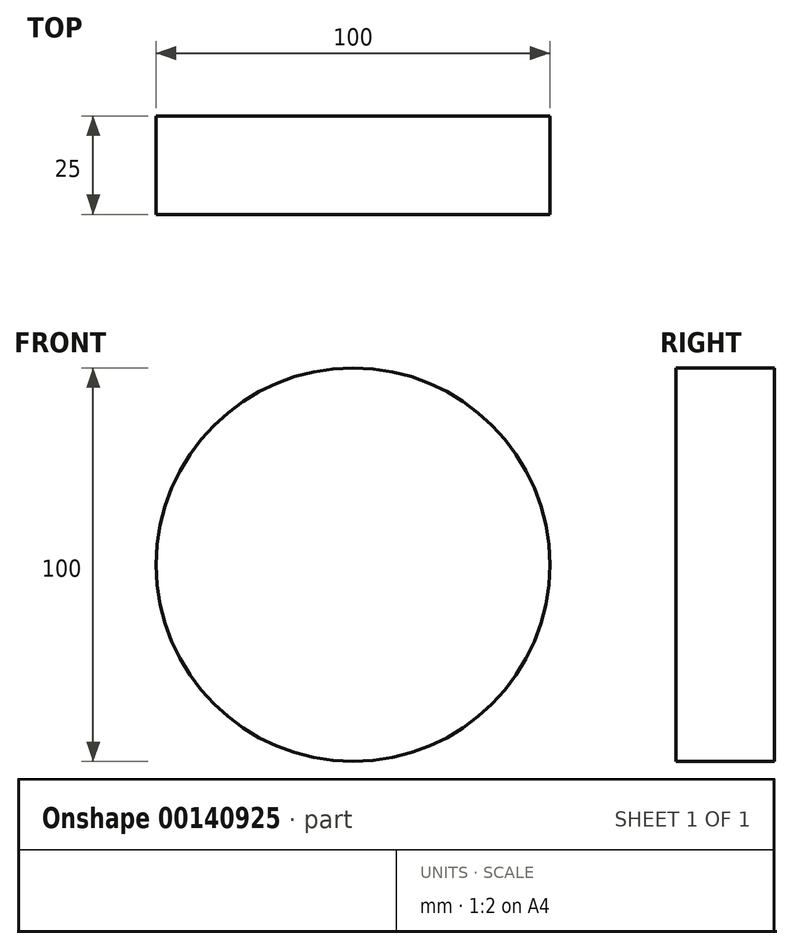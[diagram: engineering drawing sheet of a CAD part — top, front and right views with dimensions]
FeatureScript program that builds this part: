
annotation { "Feature Type Name" : "Feature", "Feature Type Description" : "" }
export const myFeature = defineFeature(function(context is Context, id is Id, definition is map)
    precondition{}
    {
        {
            var Q0;
            Q0=qCreatedBy(makeId("Front.planeOp"),FACE);
            var sketch = newSketch(context, id + "F0", { "sketchPlane" : qUnion([Q0])});
            skCircle(sketch, "E0", {"center": v(0, 0) * mm, "radius": 50 * mm});
            skSolve(sketch);
        }
        {
            var Q0;
            Q0=sQuery(id+"F0.wireOp",EDGE,"E0");
            extrude(context, id + "F1", {"bodyType" : ToolBodyType.SURFACE, "surfaceEntities" : qUnion([Q0]), "depth" : 25 * mm});
        }
    });
